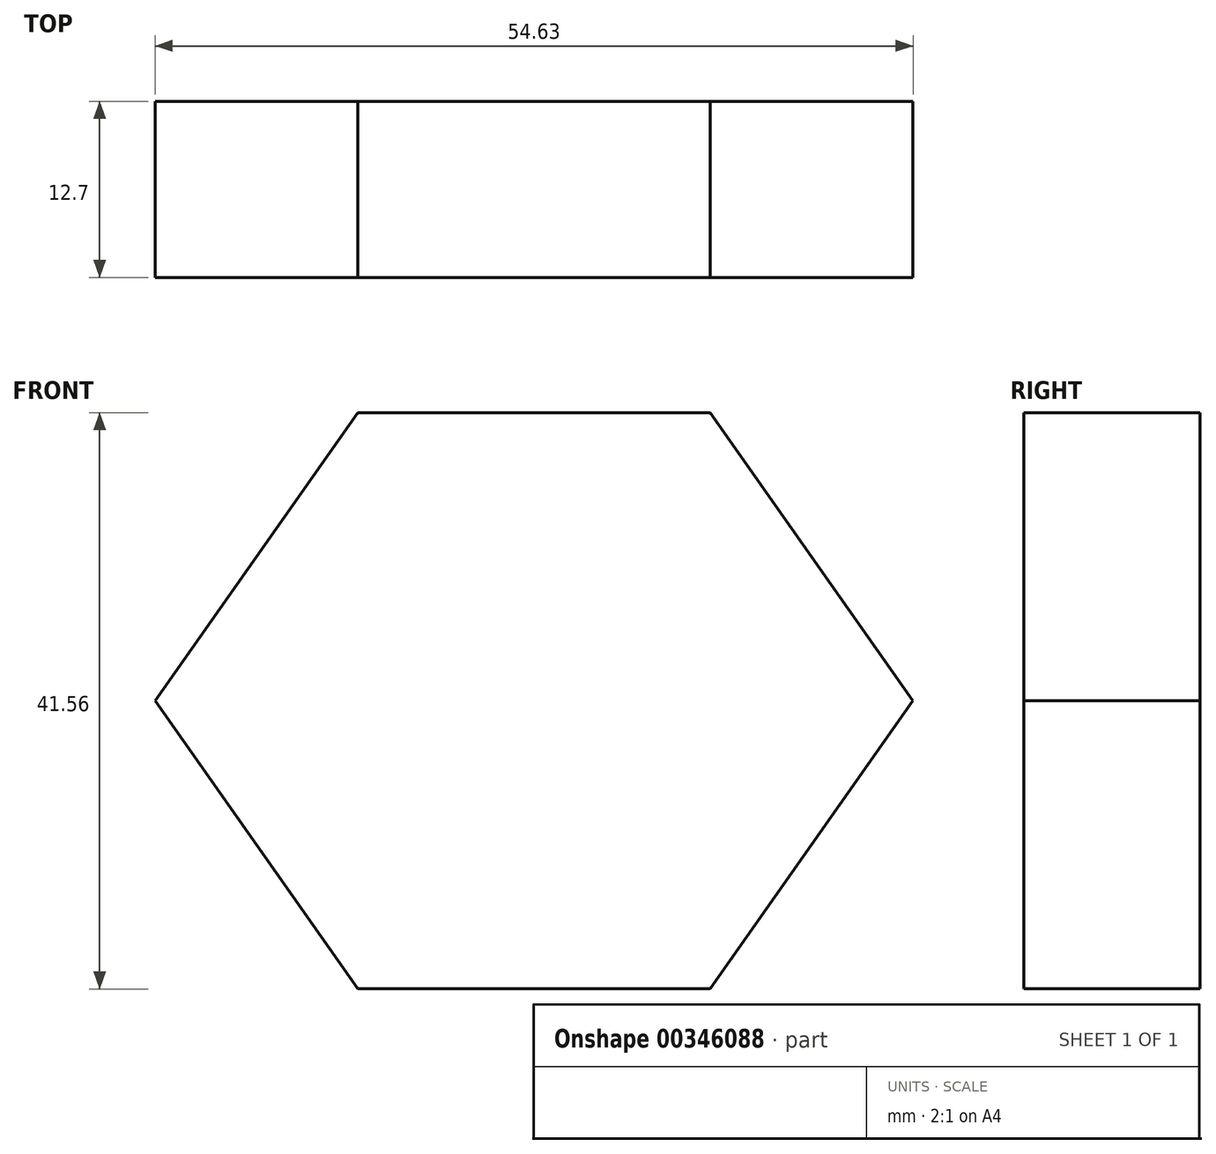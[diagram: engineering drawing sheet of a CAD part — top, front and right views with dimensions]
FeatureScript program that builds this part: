
annotation { "Feature Type Name" : "Feature", "Feature Type Description" : "" }
export const myFeature = defineFeature(function(context is Context, id is Id, definition is map)
    precondition{}
    {
        {
            var Q0;
            Q0=qCreatedBy(makeId("Front.planeOp"),FACE);
            var sketch = newSketch(context, id + "F0", { "sketchPlane" : qUnion([Q0])});
            skLineSegment(sketch, "E0", {"start": v(-17.7, 20.78) * mm, "end": v(7.7, 20.78) * mm});
            skLineSegment(sketch, "E1", {"start": v(7.7, 20.78) * mm, "end": v(22.32, 0) * mm});
            skLineSegment(sketch, "E2", {"start": v(22.32, 0) * mm, "end": v(7.7, -20.78) * mm});
            skLineSegment(sketch, "E3", {"start": v(7.7, -20.78) * mm, "end": v(-17.7, -20.78) * mm});
            skLineSegment(sketch, "E4", {"start": v(-17.7, -20.78) * mm, "end": v(-32.3, 0) * mm});
            skLineSegment(sketch, "E5", {"start": v(-32.3, 0) * mm, "end": v(-17.7, 20.78) * mm});
            skSolve(sketch);
        }
        {
            var Q0;
            Q0=makeQuery(id+"F0.imprint","IMPRINT",FACE,{"disambiguationData":[TD([[makeQuery(id+"F0.imprint","IMPRINT",EDGE,{"derivedFrom":sQuery(id+"F0.wireOp",EDGE,"E0")}),-1.0]])]});
            extrude(context, id + "F1", {"entities" : qUnion([Q0]), "depth" : 12.7 * mm});
        }
        {
            var Q0;
            Q0=qCreatedBy(makeId("Front.planeOp"),FACE);
            var sketch = newSketch(context, id + "F2", { "sketchPlane" : qUnion([Q0])});
            skCircle(sketch, "E6", {"center": v(-5.9, 0) * mm, "radius": 10.3 * mm});
            skSolve(sketch);
        }
        {
            var Q0;
            Q0=sQuery(id+"F2.wireOp",EDGE,"E6");
            extrude(context, id + "F3", {"bodyType" : ToolBodyType.SURFACE, "surfaceEntities" : qUnion([Q0]), "oppositeDirection" : true, "depth" : 63.5 * mm});
        }
    });
